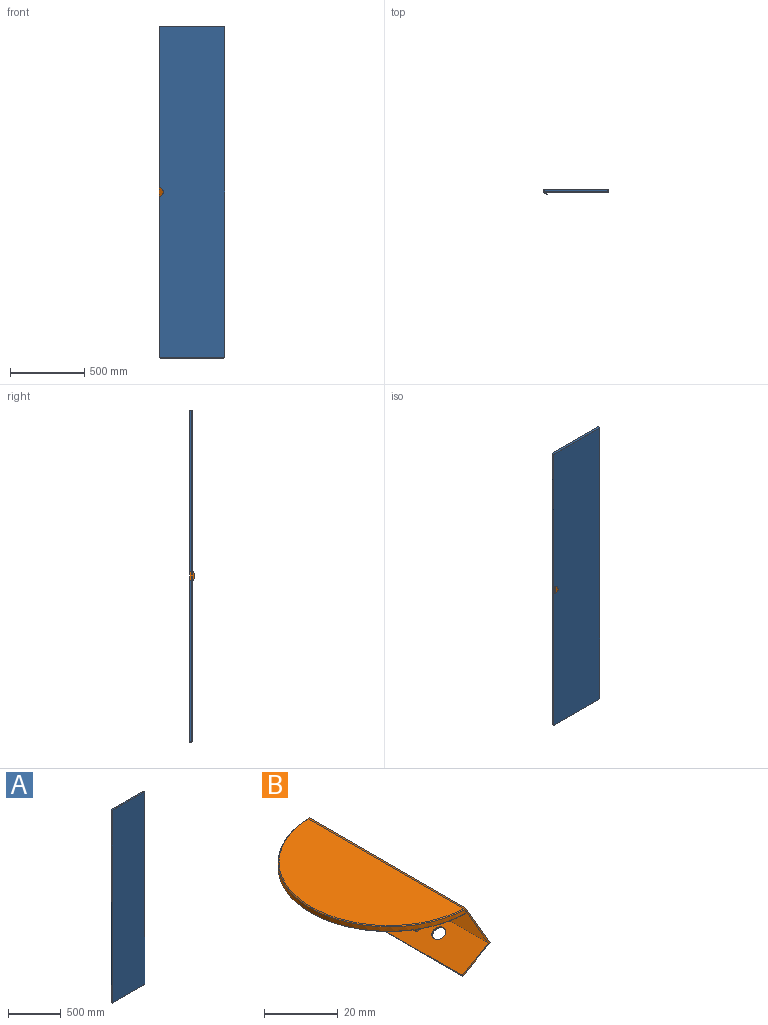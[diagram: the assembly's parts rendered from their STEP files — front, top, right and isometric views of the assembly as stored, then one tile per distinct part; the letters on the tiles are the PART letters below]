
ASSEMBLY  parts=2 mates=1
PART A: 18 faces, bbox 440.8x16x2240.8 mm
  f0: plane 430x15mm, normal (0,0,1), area 6450mm2, adj f5,f6,f9,f10
  f1: plane 2230x15mm, normal (-1,0,0), area 33450mm2, adj f5,f6,f7,f13
  f2: plane 430x15mm, normal (0,0,-1), area 6450mm2, adj f5,f7,f8,f17
  f3: plane 2230x15mm, normal (1,0,0), area 33450mm2, adj f5,f8,f9,f14
  f4: plane 2238x438mm, normal (0,-1,0), area 980230.3mm2, adj f10,f11,f12,f13,f14,f15,f16,f17
  f5: plane 2240x440mm, normal (0,1,0), area 985578.5mm2, adj f0,f1,f2,f3,f6,f7,f8,f9
  f6: cylinder r=5mm len=15mm, axis (0,-1,0), area 117.8mm2, adj f0,f1,f5,f11
  f7: cylinder r=5mm len=15mm, axis (0,1,0), area 117.8mm2, adj f1,f2,f5,f15
  f8: cylinder r=5mm len=15mm, axis (0,-1,0), area 117.8mm2, adj f2,f3,f5,f16
  f9: cylinder r=5mm len=15mm, axis (0,1,0), area 117.8mm2, adj f0,f3,f5,f12
  f10: cylinder r=1mm len=430mm, axis (1,0,0), area 675.4mm2, adj f0,f4,f11,f12
  f11: torus R=4mm, axis (0,-1,0), area 11.4mm2, adj f4,f6,f10,f13
  f12: torus R=4mm, axis (0,-1,0), area 11.4mm2, adj f4,f9,f10,f14
  f13: cylinder r=1mm len=2230mm, axis (0,0,1), area 3502.9mm2, adj f1,f4,f11,f15
  f14: cylinder r=1mm len=2230mm, axis (0,0,-1), area 3502.9mm2, adj f3,f4,f12,f16
  f15: torus R=4mm, axis (0,-1,0), area 11.4mm2, adj f4,f7,f13,f17
  f16: torus R=4mm, axis (0,-1,0), area 11.4mm2, adj f4,f8,f14,f17
  f17: cylinder r=1mm len=430mm, axis (-1,0,0), area 675.4mm2, adj f2,f4,f15,f16
PART B: 26 faces, bbox 38.7x60x22 mm
  f0: plane 1.52x0.88mm, normal (0.87,0,0.5), area 0mm2, adj f2,f4,f17
  f1: plane 1.52x0.88mm, normal (0.87,0,0.5), area 0mm2, adj f2,f4,f19
  f2: cylinder r=30mm len=60mm, axis (0,0,-1), area 139.6mm2, adj f0,f1,f4,f5
  f3: plane 59.46x28.6mm, normal (0,0,1), area 1321.6mm2, adj f5,f15
  f4: cone r=30mm half-angle=45deg, axis (0,0,1), area 33.1mm2, adj f0,f1,f2,f6,f16
  f5: cone r=29.75mm half-angle=45deg, axis (0,0,-1), area 32.4mm2, adj f2,f3,f15
  f6: plane 59.5x29.75mm, normal (0,0,-1), area 945.2mm2, adj f4,f8,f9,f10,f16
  f7: plane 46x10mm, normal (0.5,0,-0.87), area 496.8mm2, adj f8,f9,f10,f12,f14,f16
  f8: plane 41.42x5.77mm, normal (-1,0,0), area 239.2mm2, adj f6,f7,f9,f10
  f9: cylinder r=23mm len=10mm, axis (0,0,1), area 30.4mm2, adj f6,f7,f8
  f10: cylinder r=23mm len=10mm, axis (0,0,1), area 30.4mm2, adj f6,f7,f8
  f11: cone r=0mm half-angle=59deg, axis (0.5,0,-0.87), area 10mm2, adj f12
  f12: cylinder r=1.65mm len=4.85mm, axis (0.5,0,-0.87), area 38.4mm2, adj f7,f11
  f13: cone r=0mm half-angle=59deg, axis (0.5,0,-0.87), area 10mm2, adj f14
  f14: cylinder r=1.65mm len=4.85mm, axis (0.5,0,-0.87), area 38.4mm2, adj f7,f13
  f15: plane 59.97x0.25mm, normal (0.87,0,0.5), area 17.2mm2, adj f3,f5,f18
  f16: plane 59.97x14.09mm, normal (-0.87,0,-0.5), area 959.5mm2, adj f4,f6,f7,f17,f19,f23
  f17: plane 22.04x10.64mm, normal (0,1,0), area 15mm2, adj f0,f16,f18,f20,f21,f22,f23
  f18: plane 59.97x0.43mm, normal (-0.5,0,0.87), area 30mm2, adj f15,f17,f19,f20
  f19: plane 22.04x10.64mm, normal (0,-1,0), area 15mm2, adj f1,f16,f18,f20,f21,f22,f23
  f20: plane 59.97x16.04mm, normal (0.87,0,0.5), area 1110.6mm2, adj f17,f18,f19,f22
  f21: plane 59.97x0.43mm, normal (-0.87,0,-0.5), area 30mm2, adj f17,f19,f22,f23
  f22: plane 59.97x10.39mm, normal (0.5,0,-0.87), area 694.5mm2, adj f17,f19,f20,f21,f24,f25
  f23: plane 59.97x9.96mm, normal (-0.5,0,0.87), area 664.5mm2, adj f16,f17,f19,f21,f24,f25
  f24: cylinder r=2mm len=4mm, axis (0.5,0,-0.87), area 6.3mm2, adj f22,f23
  f25: cylinder r=2mm len=4mm, axis (0.5,0,-0.87), area 6.3mm2, adj f22,f23
PLACE A t=(-511.6,129.87,-178.1)mm
PLACE B rot(axis=(-0.19,-0.69,0.69),158.9deg) t=(-733.09,114.37,627.16)mm
MATE fastened B.f16 <-> A.f1  axis (1,0,0) through (-733.09,122.37,627.16)mm
